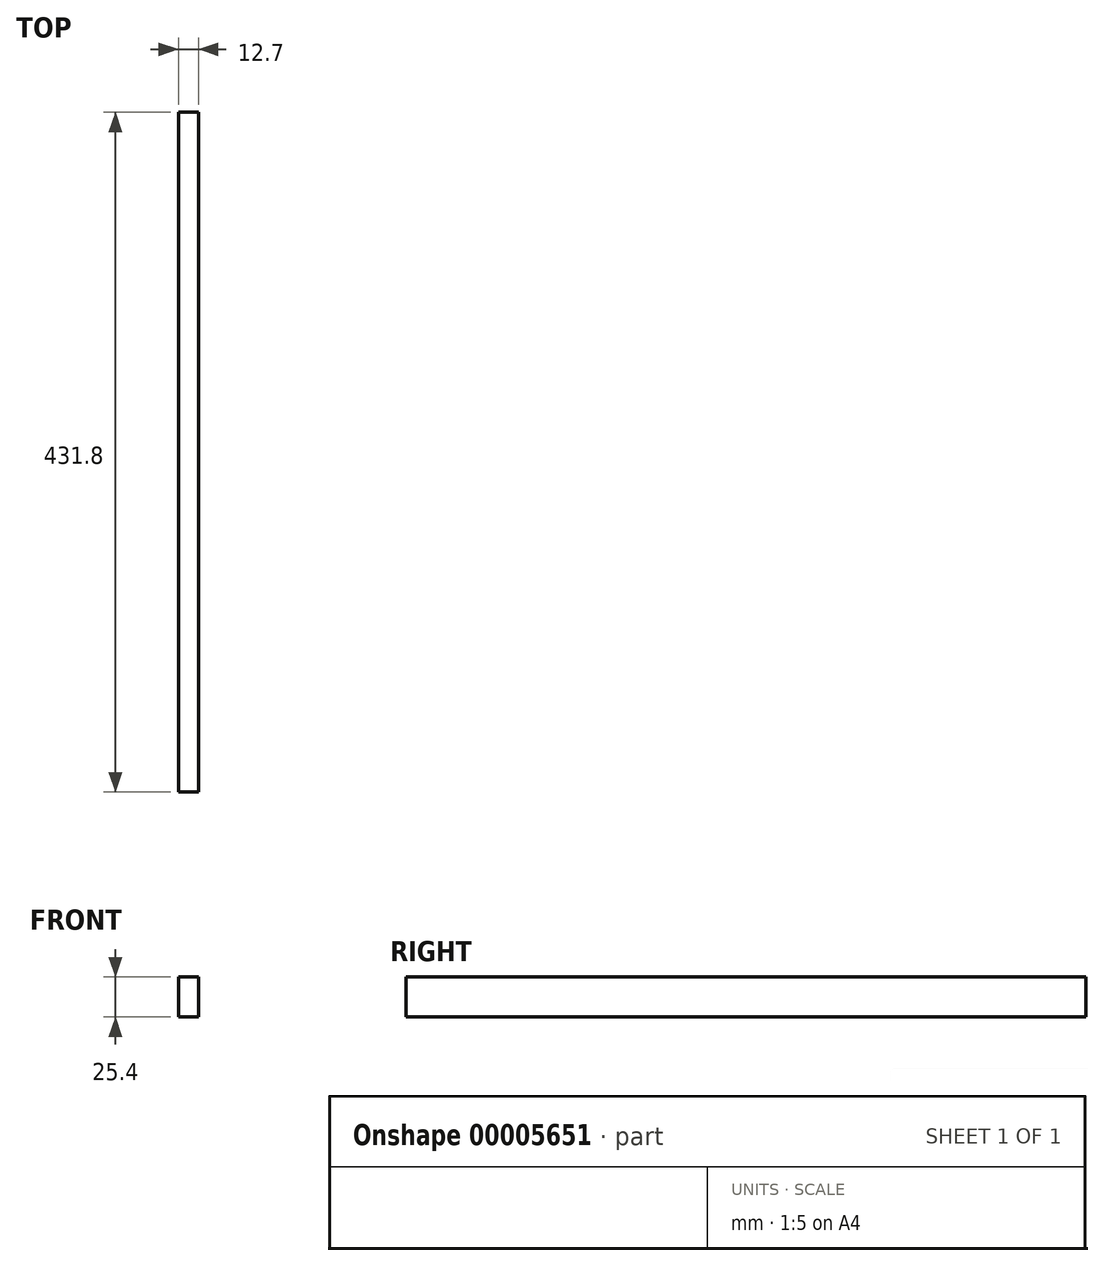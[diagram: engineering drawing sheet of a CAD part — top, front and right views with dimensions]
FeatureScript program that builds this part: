
annotation { "Feature Type Name" : "Feature", "Feature Type Description" : "" }
export const myFeature = defineFeature(function(context is Context, id is Id, definition is map)
    precondition{}
    {
        {
            var Q0;
            Q0=qCreatedBy(makeId("Top.planeOp"),FACE);
            var sketch = newSketch(context, id + "F0", { "sketchPlane" : qUnion([Q0])});
            skLineSegment(sketch, "E0.bottom", {"start": v(0, 0) * mm, "end": v(12.7, 0) * mm});
            skLineSegment(sketch, "E0.top", {"start": v(0, 431.8) * mm, "end": v(12.7, 431.8) * mm});
            skLineSegment(sketch, "E0.left", {"start": v(0, 0) * mm, "end": v(0, 431.8) * mm});
            skLineSegment(sketch, "E0.right", {"start": v(12.7, 0) * mm, "end": v(12.7, 431.8) * mm});
            skSolve(sketch);
        }
        {
            var Q0;
            Q0 = qSketchRegion(id + "F0", true);
            extrude(context, id + "F1", {"entities" : qUnion([Q0]), "depth" : 25.4 * mm});
        }
    });
